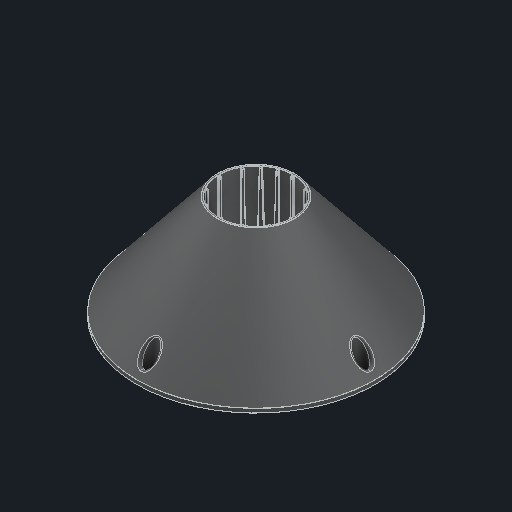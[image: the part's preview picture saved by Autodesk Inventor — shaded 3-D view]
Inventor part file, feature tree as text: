
AUTODESK INVENTOR PART (.ipt)
format: ipt  version: 2025 (Build 290162000, 162)  size: 3,986,944 bytes
history: native  units: in
note: dims shown in document units (in); Inventor stores cm internally (conversion verified against a paired STEP export)
features: fillet x1
ambient origin geometry x8: Origin, YZ Plane, XZ Plane, XY Plane, X Axis, Y Axis, Z Axis, Center Point
bodies: Solid1 (feature_tree)
feature tree (1):
  fillet  "Fillet22"  [1 undecoded]
note: 1 required parameter value undecoded (feature->parameter linkage not recoverable at this tier; creation-order binding heuristic only, values carry confidence <= 0.55)
